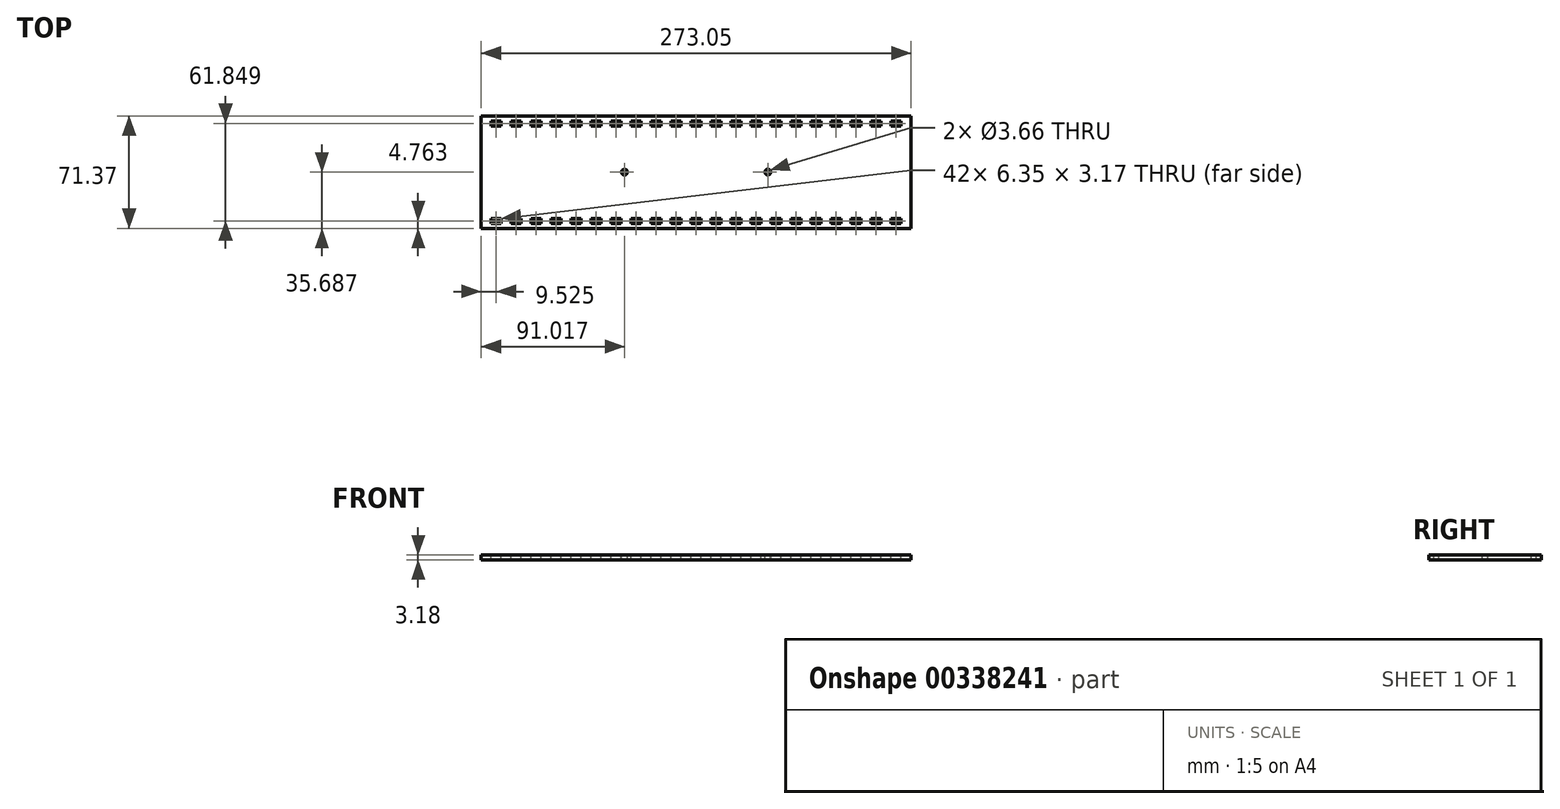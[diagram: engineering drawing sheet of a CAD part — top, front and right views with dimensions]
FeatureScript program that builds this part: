
annotation { "Feature Type Name" : "Feature", "Feature Type Description" : "" }
export const myFeature = defineFeature(function(context is Context, id is Id, definition is map)
    precondition{}
    {
        {
            var Q0;
            Q0=qCreatedBy(makeId("Top.planeOp"),FACE);
            var sketch = newSketch(context, id + "F0", { "sketchPlane" : qUnion([Q0])});
            skLineSegment(sketch, "E0.bottom", {"start": v(0, 0) * mm, "end": v(-273.05, 0) * mm});
            skLineSegment(sketch, "E0.top", {"start": v(0, 71.37) * mm, "end": v(-273.05, 71.37) * mm});
            skLineSegment(sketch, "E0.left", {"start": v(0, 0) * mm, "end": v(0, 71.37) * mm});
            skLineSegment(sketch, "E0.right", {"start": v(-273.05, 0) * mm, "end": v(-273.05, 71.37) * mm});
            skSolve(sketch);
        }
        {
            var Q0;
            Q0 = qSketchRegion(id + "F0", true);
            extrude(context, id + "F1", {"entities" : qUnion([Q0]), "depth" : 3.17 * mm});
        }
        {
            var Q0;
            Q0=makeQuery(id+"F1.opExtrude","CAP_FACE",FACE,{"disambiguationData":[OSD([sQuery(id+"F0.wireOp",EDGE,"E0.bottom"),sQuery(id+"F0.wireOp",EDGE,"E0.top"),sQuery(id+"F0.wireOp",EDGE,"E0.left"),sQuery(id+"F0.wireOp",EDGE,"E0.right")])],"isStart":false});
            var sketch = newSketch(context, id + "F2", { "sketchPlane" : qUnion([Q0])});
            skLineSegment(sketch, "E1", {"start": v(0, 4.76) * mm, "end": v(-6.35, 4.76) * mm, "construction": true});
            skLineSegment(sketch, "E2", {"start": v(0, 35.69) * mm, "end": v(-91.02, 35.69) * mm, "construction": true});
            skLineSegment(sketch, "E3", {"start": v(-91.02, 35.69) * mm, "end": v(-182.03, 35.69) * mm, "construction": true});
            skLineSegment(sketch, "E4", {"start": v(-182.03, 35.69) * mm, "end": v(-273.05, 35.69) * mm, "construction": true});
            skCircle(sketch, "E5", {"center": v(-182.03, 35.69) * mm, "radius": 1.83 * mm});
            skCircle(sketch, "E6", {"center": v(-91.02, 35.69) * mm, "radius": 1.83 * mm});
            skLineSegment(sketch, "E7.bottom", {"start": v(-6.35, 3.18) * mm, "end": v(-12.7, 3.17) * mm});
            skLineSegment(sketch, "E7.top", {"start": v(-6.35, 6.35) * mm, "end": v(-12.7, 6.35) * mm});
            skLineSegment(sketch, "E7.left", {"start": v(-6.35, 3.17) * mm, "end": v(-6.35, 6.35) * mm});
            skLineSegment(sketch, "E7.right", {"start": v(-12.7, 3.18) * mm, "end": v(-12.7, 6.35) * mm});
            skLineSegment(sketch, "E8", {"start": v(-9.53, 3.18) * mm, "end": v(-9.53, 0) * mm, "construction": true});
            skLineSegment(sketch, "E9", {"start": v(-9.53, 71.37) * mm, "end": v(-9.53, 68.2) * mm, "construction": true});
            skLineSegment(sketch, "E10.bottom", {"start": v(-12.7, 68.2) * mm, "end": v(-6.35, 68.2) * mm});
            skLineSegment(sketch, "E10.top", {"start": v(-12.7, 65.02) * mm, "end": v(-6.35, 65.02) * mm});
            skLineSegment(sketch, "E10.left", {"start": v(-12.7, 68.2) * mm, "end": v(-12.7, 65.02) * mm});
            skLineSegment(sketch, "E10.right", {"start": v(-6.35, 68.2) * mm, "end": v(-6.35, 65.02) * mm});
            skLineSegment(sketch, "E11", {"start": v(-6.35, 66.61) * mm, "end": v(0, 66.61) * mm, "construction": true});
            skLineSegment(sketch, "E12.1.0.0", {"start": v(-19.05, 66.61) * mm, "end": v(-12.7, 66.61) * mm, "construction": true});
            skLineSegment(sketch, "E12.1.0.1", {"start": v(-25.4, 68.2) * mm, "end": v(-19.05, 68.2) * mm});
            skLineSegment(sketch, "E12.1.0.2", {"start": v(-25.4, 68.2) * mm, "end": v(-25.4, 65.02) * mm});
            skLineSegment(sketch, "E12.1.0.3", {"start": v(-25.4, 65.02) * mm, "end": v(-19.05, 65.02) * mm});
            skLineSegment(sketch, "E12.1.0.4", {"start": v(-19.05, 68.2) * mm, "end": v(-19.05, 65.02) * mm});
            skLineSegment(sketch, "E12.2.0.0", {"start": v(-31.75, 66.61) * mm, "end": v(-25.4, 66.61) * mm, "construction": true});
            skLineSegment(sketch, "E12.2.0.1", {"start": v(-38.1, 68.2) * mm, "end": v(-31.75, 68.2) * mm});
            skLineSegment(sketch, "E12.2.0.2", {"start": v(-38.1, 68.2) * mm, "end": v(-38.1, 65.02) * mm});
            skLineSegment(sketch, "E12.2.0.3", {"start": v(-38.1, 65.02) * mm, "end": v(-31.75, 65.02) * mm});
            skLineSegment(sketch, "E12.2.0.4", {"start": v(-31.75, 68.2) * mm, "end": v(-31.75, 65.02) * mm});
            skLineSegment(sketch, "E12.3.0.0", {"start": v(-44.45, 66.61) * mm, "end": v(-38.1, 66.61) * mm, "construction": true});
            skLineSegment(sketch, "E12.3.0.1", {"start": v(-50.8, 68.2) * mm, "end": v(-44.45, 68.2) * mm});
            skLineSegment(sketch, "E12.3.0.2", {"start": v(-50.8, 68.2) * mm, "end": v(-50.8, 65.02) * mm});
            skLineSegment(sketch, "E12.3.0.3", {"start": v(-50.8, 65.02) * mm, "end": v(-44.45, 65.02) * mm});
            skLineSegment(sketch, "E12.3.0.4", {"start": v(-44.45, 68.2) * mm, "end": v(-44.45, 65.02) * mm});
            skLineSegment(sketch, "E12.4.0.0", {"start": v(-57.15, 66.61) * mm, "end": v(-50.8, 66.61) * mm, "construction": true});
            skLineSegment(sketch, "E12.4.0.1", {"start": v(-63.5, 68.2) * mm, "end": v(-57.15, 68.2) * mm});
            skLineSegment(sketch, "E12.4.0.2", {"start": v(-63.5, 68.2) * mm, "end": v(-63.5, 65.02) * mm});
            skLineSegment(sketch, "E12.4.0.3", {"start": v(-63.5, 65.02) * mm, "end": v(-57.15, 65.02) * mm});
            skLineSegment(sketch, "E12.4.0.4", {"start": v(-57.15, 68.2) * mm, "end": v(-57.15, 65.02) * mm});
            skLineSegment(sketch, "E12.5.0.0", {"start": v(-69.85, 66.61) * mm, "end": v(-63.5, 66.61) * mm, "construction": true});
            skLineSegment(sketch, "E12.5.0.1", {"start": v(-76.2, 68.2) * mm, "end": v(-69.85, 68.2) * mm});
            skLineSegment(sketch, "E12.5.0.2", {"start": v(-76.2, 68.2) * mm, "end": v(-76.2, 65.02) * mm});
            skLineSegment(sketch, "E12.5.0.3", {"start": v(-76.2, 65.02) * mm, "end": v(-69.85, 65.02) * mm});
            skLineSegment(sketch, "E12.5.0.4", {"start": v(-69.85, 68.2) * mm, "end": v(-69.85, 65.02) * mm});
            skLineSegment(sketch, "E12.6.0.0", {"start": v(-82.55, 66.61) * mm, "end": v(-76.2, 66.61) * mm, "construction": true});
            skLineSegment(sketch, "E12.6.0.1", {"start": v(-88.9, 68.2) * mm, "end": v(-82.55, 68.2) * mm});
            skLineSegment(sketch, "E12.6.0.2", {"start": v(-88.9, 68.2) * mm, "end": v(-88.9, 65.02) * mm});
            skLineSegment(sketch, "E12.6.0.3", {"start": v(-88.9, 65.02) * mm, "end": v(-82.55, 65.02) * mm});
            skLineSegment(sketch, "E12.6.0.4", {"start": v(-82.55, 68.2) * mm, "end": v(-82.55, 65.02) * mm});
            skLineSegment(sketch, "E12.7.0.0", {"start": v(-95.25, 66.61) * mm, "end": v(-88.9, 66.61) * mm, "construction": true});
            skLineSegment(sketch, "E12.7.0.1", {"start": v(-101.6, 68.2) * mm, "end": v(-95.25, 68.2) * mm});
            skLineSegment(sketch, "E12.7.0.2", {"start": v(-101.6, 68.2) * mm, "end": v(-101.6, 65.02) * mm});
            skLineSegment(sketch, "E12.7.0.3", {"start": v(-101.6, 65.02) * mm, "end": v(-95.25, 65.02) * mm});
            skLineSegment(sketch, "E12.7.0.4", {"start": v(-95.25, 68.2) * mm, "end": v(-95.25, 65.02) * mm});
            skLineSegment(sketch, "E12.8.0.0", {"start": v(-107.95, 66.61) * mm, "end": v(-101.6, 66.61) * mm, "construction": true});
            skLineSegment(sketch, "E12.8.0.1", {"start": v(-114.3, 68.2) * mm, "end": v(-107.95, 68.2) * mm});
            skLineSegment(sketch, "E12.8.0.2", {"start": v(-114.3, 68.2) * mm, "end": v(-114.3, 65.02) * mm});
            skLineSegment(sketch, "E12.8.0.3", {"start": v(-114.3, 65.02) * mm, "end": v(-107.95, 65.02) * mm});
            skLineSegment(sketch, "E12.8.0.4", {"start": v(-107.95, 68.2) * mm, "end": v(-107.95, 65.02) * mm});
            skLineSegment(sketch, "E12.9.0.0", {"start": v(-120.65, 66.61) * mm, "end": v(-114.3, 66.61) * mm, "construction": true});
            skLineSegment(sketch, "E12.9.0.1", {"start": v(-127, 68.2) * mm, "end": v(-120.65, 68.2) * mm});
            skLineSegment(sketch, "E12.9.0.2", {"start": v(-127, 68.2) * mm, "end": v(-127, 65.02) * mm});
            skLineSegment(sketch, "E12.9.0.3", {"start": v(-127, 65.02) * mm, "end": v(-120.65, 65.02) * mm});
            skLineSegment(sketch, "E12.9.0.4", {"start": v(-120.65, 68.2) * mm, "end": v(-120.65, 65.02) * mm});
            skLineSegment(sketch, "E12.10.0.0", {"start": v(-133.35, 66.61) * mm, "end": v(-127, 66.61) * mm, "construction": true});
            skLineSegment(sketch, "E12.10.0.1", {"start": v(-139.7, 68.2) * mm, "end": v(-133.35, 68.2) * mm});
            skLineSegment(sketch, "E12.10.0.2", {"start": v(-139.7, 68.2) * mm, "end": v(-139.7, 65.02) * mm});
            skLineSegment(sketch, "E12.10.0.3", {"start": v(-139.7, 65.02) * mm, "end": v(-133.35, 65.02) * mm});
            skLineSegment(sketch, "E12.10.0.4", {"start": v(-133.35, 68.2) * mm, "end": v(-133.35, 65.02) * mm});
            skLineSegment(sketch, "E12.11.0.0", {"start": v(-146.05, 66.61) * mm, "end": v(-139.7, 66.61) * mm, "construction": true});
            skLineSegment(sketch, "E12.11.0.1", {"start": v(-152.4, 68.2) * mm, "end": v(-146.05, 68.2) * mm});
            skLineSegment(sketch, "E12.11.0.2", {"start": v(-152.4, 68.2) * mm, "end": v(-152.4, 65.02) * mm});
            skLineSegment(sketch, "E12.11.0.3", {"start": v(-152.4, 65.02) * mm, "end": v(-146.05, 65.02) * mm});
            skLineSegment(sketch, "E12.11.0.4", {"start": v(-146.05, 68.2) * mm, "end": v(-146.05, 65.02) * mm});
            skLineSegment(sketch, "E12.12.0.0", {"start": v(-158.75, 66.61) * mm, "end": v(-152.4, 66.61) * mm, "construction": true});
            skLineSegment(sketch, "E12.12.0.1", {"start": v(-165.1, 68.2) * mm, "end": v(-158.75, 68.2) * mm});
            skLineSegment(sketch, "E12.12.0.2", {"start": v(-165.1, 68.2) * mm, "end": v(-165.1, 65.02) * mm});
            skLineSegment(sketch, "E12.12.0.3", {"start": v(-165.1, 65.02) * mm, "end": v(-158.75, 65.02) * mm});
            skLineSegment(sketch, "E12.12.0.4", {"start": v(-158.75, 68.2) * mm, "end": v(-158.75, 65.02) * mm});
            skLineSegment(sketch, "E12.13.0.0", {"start": v(-171.45, 66.61) * mm, "end": v(-165.1, 66.61) * mm, "construction": true});
            skLineSegment(sketch, "E12.13.0.1", {"start": v(-177.8, 68.2) * mm, "end": v(-171.45, 68.2) * mm});
            skLineSegment(sketch, "E12.13.0.2", {"start": v(-177.8, 68.2) * mm, "end": v(-177.8, 65.02) * mm});
            skLineSegment(sketch, "E12.13.0.3", {"start": v(-177.8, 65.02) * mm, "end": v(-171.45, 65.02) * mm});
            skLineSegment(sketch, "E12.13.0.4", {"start": v(-171.45, 68.2) * mm, "end": v(-171.45, 65.02) * mm});
            skLineSegment(sketch, "E12.14.0.0", {"start": v(-184.15, 66.61) * mm, "end": v(-177.8, 66.61) * mm, "construction": true});
            skLineSegment(sketch, "E12.14.0.1", {"start": v(-190.5, 68.2) * mm, "end": v(-184.15, 68.2) * mm});
            skLineSegment(sketch, "E12.14.0.2", {"start": v(-190.5, 68.2) * mm, "end": v(-190.5, 65.02) * mm});
            skLineSegment(sketch, "E12.14.0.3", {"start": v(-190.5, 65.02) * mm, "end": v(-184.15, 65.02) * mm});
            skLineSegment(sketch, "E12.14.0.4", {"start": v(-184.15, 68.2) * mm, "end": v(-184.15, 65.02) * mm});
            skLineSegment(sketch, "E12.15.0.0", {"start": v(-196.85, 66.61) * mm, "end": v(-190.5, 66.61) * mm, "construction": true});
            skLineSegment(sketch, "E12.15.0.1", {"start": v(-203.2, 68.2) * mm, "end": v(-196.85, 68.2) * mm});
            skLineSegment(sketch, "E12.15.0.2", {"start": v(-203.2, 68.2) * mm, "end": v(-203.2, 65.02) * mm});
            skLineSegment(sketch, "E12.15.0.3", {"start": v(-203.2, 65.02) * mm, "end": v(-196.85, 65.02) * mm});
            skLineSegment(sketch, "E12.15.0.4", {"start": v(-196.85, 68.2) * mm, "end": v(-196.85, 65.02) * mm});
            skLineSegment(sketch, "E12.16.0.0", {"start": v(-209.55, 66.61) * mm, "end": v(-203.2, 66.61) * mm, "construction": true});
            skLineSegment(sketch, "E12.16.0.1", {"start": v(-215.9, 68.2) * mm, "end": v(-209.55, 68.2) * mm});
            skLineSegment(sketch, "E12.16.0.2", {"start": v(-215.9, 68.2) * mm, "end": v(-215.9, 65.02) * mm});
            skLineSegment(sketch, "E12.16.0.3", {"start": v(-215.9, 65.02) * mm, "end": v(-209.55, 65.02) * mm});
            skLineSegment(sketch, "E12.16.0.4", {"start": v(-209.55, 68.2) * mm, "end": v(-209.55, 65.02) * mm});
            skLineSegment(sketch, "E12.17.0.0", {"start": v(-222.25, 66.61) * mm, "end": v(-215.9, 66.61) * mm, "construction": true});
            skLineSegment(sketch, "E12.17.0.1", {"start": v(-228.6, 68.2) * mm, "end": v(-222.25, 68.2) * mm});
            skLineSegment(sketch, "E12.17.0.2", {"start": v(-228.6, 68.2) * mm, "end": v(-228.6, 65.02) * mm});
            skLineSegment(sketch, "E12.17.0.3", {"start": v(-228.6, 65.02) * mm, "end": v(-222.25, 65.02) * mm});
            skLineSegment(sketch, "E12.17.0.4", {"start": v(-222.25, 68.2) * mm, "end": v(-222.25, 65.02) * mm});
            skLineSegment(sketch, "E12.18.0.0", {"start": v(-234.95, 66.61) * mm, "end": v(-228.6, 66.61) * mm, "construction": true});
            skLineSegment(sketch, "E12.18.0.1", {"start": v(-241.3, 68.2) * mm, "end": v(-234.95, 68.2) * mm});
            skLineSegment(sketch, "E12.18.0.2", {"start": v(-241.3, 68.2) * mm, "end": v(-241.3, 65.02) * mm});
            skLineSegment(sketch, "E12.18.0.3", {"start": v(-241.3, 65.02) * mm, "end": v(-234.95, 65.02) * mm});
            skLineSegment(sketch, "E12.18.0.4", {"start": v(-234.95, 68.2) * mm, "end": v(-234.95, 65.02) * mm});
            skLineSegment(sketch, "E12.19.0.0", {"start": v(-247.65, 66.61) * mm, "end": v(-241.3, 66.61) * mm, "construction": true});
            skLineSegment(sketch, "E12.19.0.1", {"start": v(-254, 68.2) * mm, "end": v(-247.65, 68.2) * mm});
            skLineSegment(sketch, "E12.19.0.2", {"start": v(-254, 68.2) * mm, "end": v(-254, 65.02) * mm});
            skLineSegment(sketch, "E12.19.0.3", {"start": v(-254, 65.02) * mm, "end": v(-247.65, 65.02) * mm});
            skLineSegment(sketch, "E12.19.0.4", {"start": v(-247.65, 68.2) * mm, "end": v(-247.65, 65.02) * mm});
            skLineSegment(sketch, "E12.20.0.0", {"start": v(-260.35, 66.61) * mm, "end": v(-254, 66.61) * mm, "construction": true});
            skLineSegment(sketch, "E12.20.0.1", {"start": v(-266.7, 68.2) * mm, "end": v(-260.35, 68.2) * mm});
            skLineSegment(sketch, "E12.20.0.2", {"start": v(-266.7, 68.2) * mm, "end": v(-266.7, 65.02) * mm});
            skLineSegment(sketch, "E12.20.0.3", {"start": v(-266.7, 65.02) * mm, "end": v(-260.35, 65.02) * mm});
            skLineSegment(sketch, "E12.20.0.4", {"start": v(-260.35, 68.2) * mm, "end": v(-260.35, 65.02) * mm});
            skLineSegment(sketch, "E12.21.0.0", {"start": v(-273.05, 66.61) * mm, "end": v(-266.7, 66.61) * mm, "construction": true});
            skLineSegment(sketch, "E12.21.0.1", {"start": v(-279.4, 68.2) * mm, "end": v(-273.05, 68.2) * mm});
            skLineSegment(sketch, "E12.21.0.2", {"start": v(-279.4, 68.2) * mm, "end": v(-279.4, 65.02) * mm});
            skLineSegment(sketch, "E12.21.0.3", {"start": v(-279.4, 65.02) * mm, "end": v(-273.05, 65.02) * mm});
            skLineSegment(sketch, "E12.21.0.4", {"start": v(-273.05, 68.2) * mm, "end": v(-273.05, 65.02) * mm});
            skLineSegment(sketch, "E12.direction1", {"start": v(-12.7, 65.02) * mm, "end": v(-25.4, 65.02) * mm, "construction": true});
            skLineSegment(sketch, "E13.1.0.0", {"start": v(-12.7, 4.76) * mm, "end": v(-19.05, 4.76) * mm, "construction": true});
            skLineSegment(sketch, "E13.1.0.1", {"start": v(-19.05, 6.35) * mm, "end": v(-25.4, 6.35) * mm});
            skLineSegment(sketch, "E13.1.0.2", {"start": v(-19.05, 3.17) * mm, "end": v(-19.05, 6.35) * mm});
            skLineSegment(sketch, "E13.1.0.3", {"start": v(-25.4, 3.18) * mm, "end": v(-25.4, 6.35) * mm});
            skLineSegment(sketch, "E13.1.0.4", {"start": v(-19.05, 3.18) * mm, "end": v(-25.4, 3.17) * mm});
            skLineSegment(sketch, "E13.2.0.0", {"start": v(-25.4, 4.76) * mm, "end": v(-31.75, 4.76) * mm, "construction": true});
            skLineSegment(sketch, "E13.2.0.1", {"start": v(-31.75, 6.35) * mm, "end": v(-38.1, 6.35) * mm});
            skLineSegment(sketch, "E13.2.0.2", {"start": v(-31.75, 3.17) * mm, "end": v(-31.75, 6.35) * mm});
            skLineSegment(sketch, "E13.2.0.3", {"start": v(-38.1, 3.18) * mm, "end": v(-38.1, 6.35) * mm});
            skLineSegment(sketch, "E13.2.0.4", {"start": v(-31.75, 3.18) * mm, "end": v(-38.1, 3.17) * mm});
            skLineSegment(sketch, "E13.3.0.0", {"start": v(-38.1, 4.76) * mm, "end": v(-44.45, 4.76) * mm, "construction": true});
            skLineSegment(sketch, "E13.3.0.1", {"start": v(-44.45, 6.35) * mm, "end": v(-50.8, 6.35) * mm});
            skLineSegment(sketch, "E13.3.0.2", {"start": v(-44.45, 3.17) * mm, "end": v(-44.45, 6.35) * mm});
            skLineSegment(sketch, "E13.3.0.3", {"start": v(-50.8, 3.18) * mm, "end": v(-50.8, 6.35) * mm});
            skLineSegment(sketch, "E13.3.0.4", {"start": v(-44.45, 3.18) * mm, "end": v(-50.8, 3.17) * mm});
            skLineSegment(sketch, "E13.4.0.0", {"start": v(-50.8, 4.76) * mm, "end": v(-57.15, 4.76) * mm, "construction": true});
            skLineSegment(sketch, "E13.4.0.1", {"start": v(-57.15, 6.35) * mm, "end": v(-63.5, 6.35) * mm});
            skLineSegment(sketch, "E13.4.0.2", {"start": v(-57.15, 3.17) * mm, "end": v(-57.15, 6.35) * mm});
            skLineSegment(sketch, "E13.4.0.3", {"start": v(-63.5, 3.18) * mm, "end": v(-63.5, 6.35) * mm});
            skLineSegment(sketch, "E13.4.0.4", {"start": v(-57.15, 3.18) * mm, "end": v(-63.5, 3.17) * mm});
            skLineSegment(sketch, "E13.5.0.0", {"start": v(-63.5, 4.76) * mm, "end": v(-69.85, 4.76) * mm, "construction": true});
            skLineSegment(sketch, "E13.5.0.1", {"start": v(-69.85, 6.35) * mm, "end": v(-76.2, 6.35) * mm});
            skLineSegment(sketch, "E13.5.0.2", {"start": v(-69.85, 3.17) * mm, "end": v(-69.85, 6.35) * mm});
            skLineSegment(sketch, "E13.5.0.3", {"start": v(-76.2, 3.18) * mm, "end": v(-76.2, 6.35) * mm});
            skLineSegment(sketch, "E13.5.0.4", {"start": v(-69.85, 3.18) * mm, "end": v(-76.2, 3.17) * mm});
            skLineSegment(sketch, "E13.6.0.0", {"start": v(-76.2, 4.76) * mm, "end": v(-82.55, 4.76) * mm, "construction": true});
            skLineSegment(sketch, "E13.6.0.1", {"start": v(-82.55, 6.35) * mm, "end": v(-88.9, 6.35) * mm});
            skLineSegment(sketch, "E13.6.0.2", {"start": v(-82.55, 3.17) * mm, "end": v(-82.55, 6.35) * mm});
            skLineSegment(sketch, "E13.6.0.3", {"start": v(-88.9, 3.18) * mm, "end": v(-88.9, 6.35) * mm});
            skLineSegment(sketch, "E13.6.0.4", {"start": v(-82.55, 3.18) * mm, "end": v(-88.9, 3.17) * mm});
            skLineSegment(sketch, "E13.7.0.0", {"start": v(-88.9, 4.76) * mm, "end": v(-95.25, 4.76) * mm, "construction": true});
            skLineSegment(sketch, "E13.7.0.1", {"start": v(-95.25, 6.35) * mm, "end": v(-101.6, 6.35) * mm});
            skLineSegment(sketch, "E13.7.0.2", {"start": v(-95.25, 3.17) * mm, "end": v(-95.25, 6.35) * mm});
            skLineSegment(sketch, "E13.7.0.3", {"start": v(-101.6, 3.18) * mm, "end": v(-101.6, 6.35) * mm});
            skLineSegment(sketch, "E13.7.0.4", {"start": v(-95.25, 3.18) * mm, "end": v(-101.6, 3.17) * mm});
            skLineSegment(sketch, "E13.8.0.0", {"start": v(-101.6, 4.76) * mm, "end": v(-107.95, 4.76) * mm, "construction": true});
            skLineSegment(sketch, "E13.8.0.1", {"start": v(-107.95, 6.35) * mm, "end": v(-114.3, 6.35) * mm});
            skLineSegment(sketch, "E13.8.0.2", {"start": v(-107.95, 3.17) * mm, "end": v(-107.95, 6.35) * mm});
            skLineSegment(sketch, "E13.8.0.3", {"start": v(-114.3, 3.18) * mm, "end": v(-114.3, 6.35) * mm});
            skLineSegment(sketch, "E13.8.0.4", {"start": v(-107.95, 3.18) * mm, "end": v(-114.3, 3.17) * mm});
            skLineSegment(sketch, "E13.9.0.0", {"start": v(-114.3, 4.76) * mm, "end": v(-120.65, 4.76) * mm, "construction": true});
            skLineSegment(sketch, "E13.9.0.1", {"start": v(-120.65, 6.35) * mm, "end": v(-127, 6.35) * mm});
            skLineSegment(sketch, "E13.9.0.2", {"start": v(-120.65, 3.17) * mm, "end": v(-120.65, 6.35) * mm});
            skLineSegment(sketch, "E13.9.0.3", {"start": v(-127, 3.18) * mm, "end": v(-127, 6.35) * mm});
            skLineSegment(sketch, "E13.9.0.4", {"start": v(-120.65, 3.18) * mm, "end": v(-127, 3.17) * mm});
            skLineSegment(sketch, "E13.10.0.0", {"start": v(-127, 4.76) * mm, "end": v(-133.35, 4.76) * mm, "construction": true});
            skLineSegment(sketch, "E13.10.0.1", {"start": v(-133.35, 6.35) * mm, "end": v(-139.7, 6.35) * mm});
            skLineSegment(sketch, "E13.10.0.2", {"start": v(-133.35, 3.17) * mm, "end": v(-133.35, 6.35) * mm});
            skLineSegment(sketch, "E13.10.0.3", {"start": v(-139.7, 3.18) * mm, "end": v(-139.7, 6.35) * mm});
            skLineSegment(sketch, "E13.10.0.4", {"start": v(-133.35, 3.18) * mm, "end": v(-139.7, 3.17) * mm});
            skLineSegment(sketch, "E13.11.0.0", {"start": v(-139.7, 4.76) * mm, "end": v(-146.05, 4.76) * mm, "construction": true});
            skLineSegment(sketch, "E13.11.0.1", {"start": v(-146.05, 6.35) * mm, "end": v(-152.4, 6.35) * mm});
            skLineSegment(sketch, "E13.11.0.2", {"start": v(-146.05, 3.17) * mm, "end": v(-146.05, 6.35) * mm});
            skLineSegment(sketch, "E13.11.0.3", {"start": v(-152.4, 3.18) * mm, "end": v(-152.4, 6.35) * mm});
            skLineSegment(sketch, "E13.11.0.4", {"start": v(-146.05, 3.18) * mm, "end": v(-152.4, 3.17) * mm});
            skLineSegment(sketch, "E13.12.0.0", {"start": v(-152.4, 4.76) * mm, "end": v(-158.75, 4.76) * mm, "construction": true});
            skLineSegment(sketch, "E13.12.0.1", {"start": v(-158.75, 6.35) * mm, "end": v(-165.1, 6.35) * mm});
            skLineSegment(sketch, "E13.12.0.2", {"start": v(-158.75, 3.17) * mm, "end": v(-158.75, 6.35) * mm});
            skLineSegment(sketch, "E13.12.0.3", {"start": v(-165.1, 3.18) * mm, "end": v(-165.1, 6.35) * mm});
            skLineSegment(sketch, "E13.12.0.4", {"start": v(-158.75, 3.18) * mm, "end": v(-165.1, 3.17) * mm});
            skLineSegment(sketch, "E13.13.0.0", {"start": v(-165.1, 4.76) * mm, "end": v(-171.45, 4.76) * mm, "construction": true});
            skLineSegment(sketch, "E13.13.0.1", {"start": v(-171.45, 6.35) * mm, "end": v(-177.8, 6.35) * mm});
            skLineSegment(sketch, "E13.13.0.2", {"start": v(-171.45, 3.17) * mm, "end": v(-171.45, 6.35) * mm});
            skLineSegment(sketch, "E13.13.0.3", {"start": v(-177.8, 3.18) * mm, "end": v(-177.8, 6.35) * mm});
            skLineSegment(sketch, "E13.13.0.4", {"start": v(-171.45, 3.18) * mm, "end": v(-177.8, 3.17) * mm});
            skLineSegment(sketch, "E13.14.0.0", {"start": v(-177.8, 4.76) * mm, "end": v(-184.15, 4.76) * mm, "construction": true});
            skLineSegment(sketch, "E13.14.0.1", {"start": v(-184.15, 6.35) * mm, "end": v(-190.5, 6.35) * mm});
            skLineSegment(sketch, "E13.14.0.2", {"start": v(-184.15, 3.17) * mm, "end": v(-184.15, 6.35) * mm});
            skLineSegment(sketch, "E13.14.0.3", {"start": v(-190.5, 3.18) * mm, "end": v(-190.5, 6.35) * mm});
            skLineSegment(sketch, "E13.14.0.4", {"start": v(-184.15, 3.18) * mm, "end": v(-190.5, 3.17) * mm});
            skLineSegment(sketch, "E13.15.0.0", {"start": v(-190.5, 4.76) * mm, "end": v(-196.85, 4.76) * mm, "construction": true});
            skLineSegment(sketch, "E13.15.0.1", {"start": v(-196.85, 6.35) * mm, "end": v(-203.2, 6.35) * mm});
            skLineSegment(sketch, "E13.15.0.2", {"start": v(-196.85, 3.17) * mm, "end": v(-196.85, 6.35) * mm});
            skLineSegment(sketch, "E13.15.0.3", {"start": v(-203.2, 3.18) * mm, "end": v(-203.2, 6.35) * mm});
            skLineSegment(sketch, "E13.15.0.4", {"start": v(-196.85, 3.18) * mm, "end": v(-203.2, 3.17) * mm});
            skLineSegment(sketch, "E13.16.0.0", {"start": v(-203.2, 4.76) * mm, "end": v(-209.55, 4.76) * mm, "construction": true});
            skLineSegment(sketch, "E13.16.0.1", {"start": v(-209.55, 6.35) * mm, "end": v(-215.9, 6.35) * mm});
            skLineSegment(sketch, "E13.16.0.2", {"start": v(-209.55, 3.17) * mm, "end": v(-209.55, 6.35) * mm});
            skLineSegment(sketch, "E13.16.0.3", {"start": v(-215.9, 3.18) * mm, "end": v(-215.9, 6.35) * mm});
            skLineSegment(sketch, "E13.16.0.4", {"start": v(-209.55, 3.18) * mm, "end": v(-215.9, 3.17) * mm});
            skLineSegment(sketch, "E13.17.0.0", {"start": v(-215.9, 4.76) * mm, "end": v(-222.25, 4.76) * mm, "construction": true});
            skLineSegment(sketch, "E13.17.0.1", {"start": v(-222.25, 6.35) * mm, "end": v(-228.6, 6.35) * mm});
            skLineSegment(sketch, "E13.17.0.2", {"start": v(-222.25, 3.17) * mm, "end": v(-222.25, 6.35) * mm});
            skLineSegment(sketch, "E13.17.0.3", {"start": v(-228.6, 3.18) * mm, "end": v(-228.6, 6.35) * mm});
            skLineSegment(sketch, "E13.17.0.4", {"start": v(-222.25, 3.18) * mm, "end": v(-228.6, 3.17) * mm});
            skLineSegment(sketch, "E13.18.0.0", {"start": v(-228.6, 4.76) * mm, "end": v(-234.95, 4.76) * mm, "construction": true});
            skLineSegment(sketch, "E13.18.0.1", {"start": v(-234.95, 6.35) * mm, "end": v(-241.3, 6.35) * mm});
            skLineSegment(sketch, "E13.18.0.2", {"start": v(-234.95, 3.17) * mm, "end": v(-234.95, 6.35) * mm});
            skLineSegment(sketch, "E13.18.0.3", {"start": v(-241.3, 3.18) * mm, "end": v(-241.3, 6.35) * mm});
            skLineSegment(sketch, "E13.18.0.4", {"start": v(-234.95, 3.18) * mm, "end": v(-241.3, 3.17) * mm});
            skLineSegment(sketch, "E13.19.0.0", {"start": v(-241.3, 4.76) * mm, "end": v(-247.65, 4.76) * mm, "construction": true});
            skLineSegment(sketch, "E13.19.0.1", {"start": v(-247.65, 6.35) * mm, "end": v(-254, 6.35) * mm});
            skLineSegment(sketch, "E13.19.0.2", {"start": v(-247.65, 3.17) * mm, "end": v(-247.65, 6.35) * mm});
            skLineSegment(sketch, "E13.19.0.3", {"start": v(-254, 3.18) * mm, "end": v(-254, 6.35) * mm});
            skLineSegment(sketch, "E13.19.0.4", {"start": v(-247.65, 3.18) * mm, "end": v(-254, 3.17) * mm});
            skLineSegment(sketch, "E13.20.0.0", {"start": v(-254, 4.76) * mm, "end": v(-260.35, 4.76) * mm, "construction": true});
            skLineSegment(sketch, "E13.20.0.1", {"start": v(-260.35, 6.35) * mm, "end": v(-266.7, 6.35) * mm});
            skLineSegment(sketch, "E13.20.0.2", {"start": v(-260.35, 3.17) * mm, "end": v(-260.35, 6.35) * mm});
            skLineSegment(sketch, "E13.20.0.3", {"start": v(-266.7, 3.18) * mm, "end": v(-266.7, 6.35) * mm});
            skLineSegment(sketch, "E13.20.0.4", {"start": v(-260.35, 3.18) * mm, "end": v(-266.7, 3.17) * mm});
            skLineSegment(sketch, "E13.21.0.0", {"start": v(-266.7, 4.76) * mm, "end": v(-273.05, 4.76) * mm, "construction": true});
            skLineSegment(sketch, "E13.21.0.1", {"start": v(-273.05, 6.35) * mm, "end": v(-279.4, 6.35) * mm});
            skLineSegment(sketch, "E13.21.0.2", {"start": v(-273.05, 3.17) * mm, "end": v(-273.05, 6.35) * mm});
            skLineSegment(sketch, "E13.21.0.3", {"start": v(-279.4, 3.18) * mm, "end": v(-279.4, 6.35) * mm});
            skLineSegment(sketch, "E13.21.0.4", {"start": v(-273.05, 3.18) * mm, "end": v(-279.4, 3.17) * mm});
            skLineSegment(sketch, "E13.direction1", {"start": v(-12.7, 3.17) * mm, "end": v(-25.4, 3.17) * mm, "construction": true});
            skSolve(sketch);
        }
        {
            var Q0;
            Q0 = qSketchRegion(id + "F2", true);
            var Q1;
            Q1=makeQuery(id+"F1.opExtrude","CAP_FACE",FACE,{"disambiguationData":[OSD([sQuery(id+"F0.wireOp",EDGE,"E0.bottom"),sQuery(id+"F0.wireOp",EDGE,"E0.top"),sQuery(id+"F0.wireOp",EDGE,"E0.left"),sQuery(id+"F0.wireOp",EDGE,"E0.right")])],"isStart":true});
            extrude(context, id + "F3", {"entities" : qUnion([Q0]), "operationType" : NewBodyOperationType.REMOVE, "endBound" : BoundingType.UP_TO_SURFACE, "oppositeDirection" : true, "endBoundEntityFace" : qUnion([Q1]), "depth" : 25.4 * mm});
        }
    });
